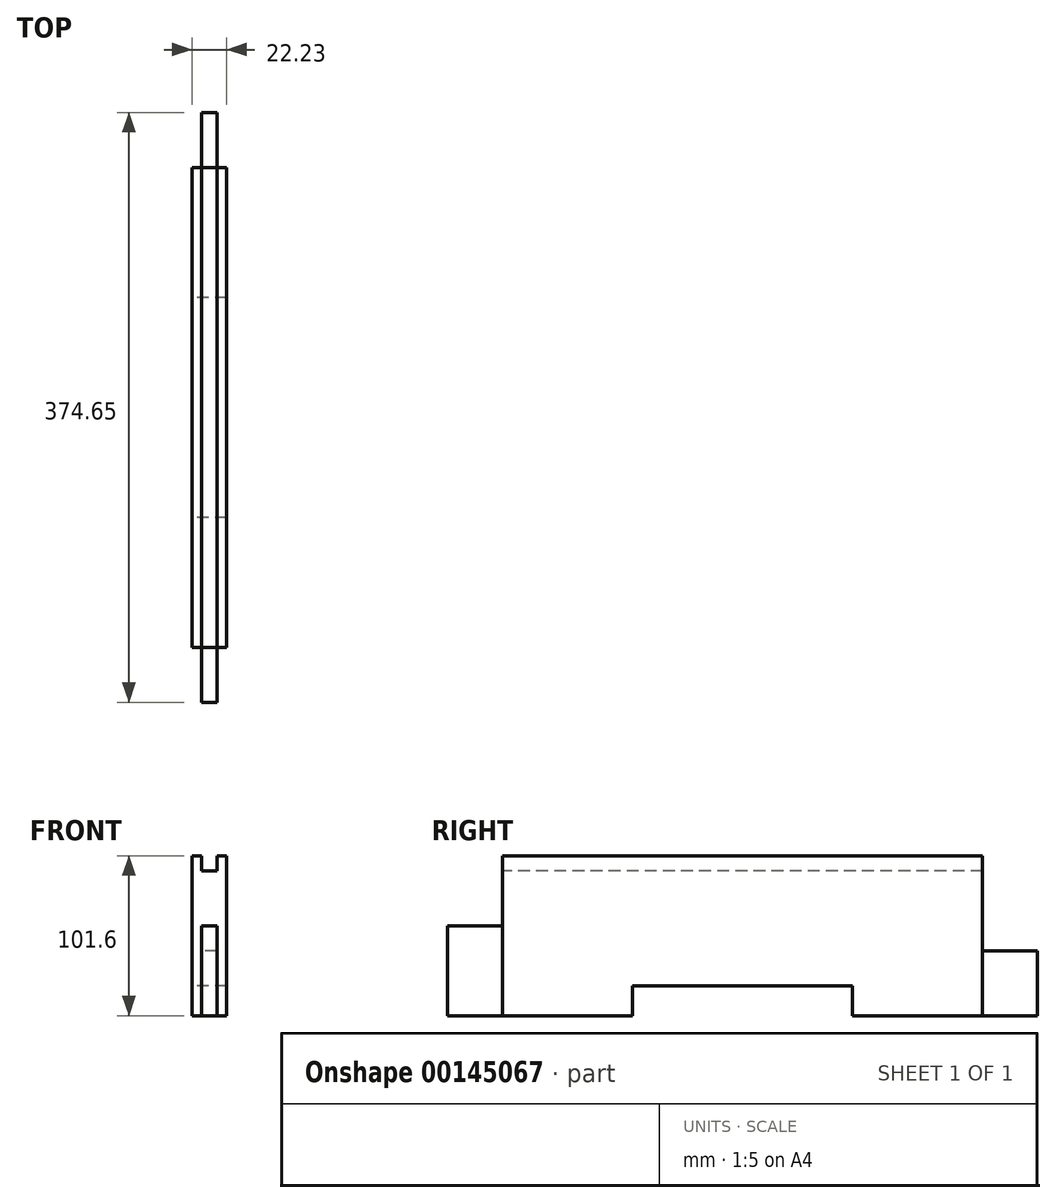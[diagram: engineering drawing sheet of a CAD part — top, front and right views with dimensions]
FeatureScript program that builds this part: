
annotation { "Feature Type Name" : "Feature", "Feature Type Description" : "" }
export const myFeature = defineFeature(function(context is Context, id is Id, definition is map)
    precondition{}
    {
        {
            var Q0;
            Q0=qCreatedBy(makeId("Right.planeOp"),FACE);
            var sketch = newSketch(context, id + "F0", { "sketchPlane" : qUnion([Q0])});
            skLineSegment(sketch, "E0.bottom", {"start": v(0, 0) * mm, "end": v(374.65, 0) * mm});
            skLineSegment(sketch, "E0.top", {"start": v(0, 101.6) * mm, "end": v(374.65, 101.6) * mm});
            skLineSegment(sketch, "E0.left", {"start": v(0, 0) * mm, "end": v(0, 101.6) * mm});
            skLineSegment(sketch, "E0.right", {"start": v(374.65, 0) * mm, "end": v(374.65, 101.6) * mm});
            skSolve(sketch);
        }
        {
            var Q0;
            Q0=makeQuery(id+"F0.imprint","IMPRINT",FACE,{"disambiguationData":[TD([[makeQuery(id+"F0.imprint","IMPRINT",EDGE,{"derivedFrom":sQuery(id+"F0.wireOp",EDGE,"E0.bottom")}),1.0]])]});
            extrude(context, id + "F1", {"entities" : qUnion([Q0]), "depth" : 22.22 * mm, "offsetDistance" : 25.4 * mm});
        }
        {
            var Q0;
            Q0=makeQuery(id+"F1.opExtrude","SWEPT_FACE",FACE,{"disambiguationData":[OSD([sQuery(id+"F0.wireOp",EDGE,"E0.top")])]});
            var sketch = newSketch(context, id + "F2", { "sketchPlane" : qUnion([Q0])});
            skLineSegment(sketch, "E1.bottom", {"start": v(15.87, 374.65) * mm, "end": v(6.35, 374.65) * mm});
            skLineSegment(sketch, "E1.top", {"start": v(15.88, 0) * mm, "end": v(6.35, 0) * mm});
            skLineSegment(sketch, "E1.left", {"start": v(15.87, 374.65) * mm, "end": v(15.88, 0) * mm});
            skLineSegment(sketch, "E1.right", {"start": v(6.35, 374.65) * mm, "end": v(6.35, 0) * mm});
            skLineSegment(sketch, "E2", {"start": v(22.23, 339.73) * mm, "end": v(0, 339.73) * mm});
            skLineSegment(sketch, "E3", {"start": v(22.23, 34.93) * mm, "end": v(0, 34.93) * mm});
            skSolve(sketch);
        }
        {
            var Q0;
            {var subQ0=sQuery(id+"F2.wireOp",EDGE,"E1.bottom");Q0=makeQuery(id+"F2.imprint","IMPRINT",FACE,{"disambiguationData":[TD([[makeQuery(id+"F2.imprint","IMPRINT",EDGE,{"derivedFrom":subQ0}),1.0]])]});}
            var Q1;
            {var subQ0=sQuery(id+"F2.wireOp",EDGE,"E2");var subQ1=sQuery(id+"F2.wireOp",EDGE,"E1.left");var subQ2=makeQuery(id+"F2.imprint","INTERSECT",VERTEX,{"derivedFrom":[subQ1,subQ0]});Q1=makeQuery(id+"F2.imprint","IMPRINT",FACE,{"disambiguationData":[TD([[makeQuery(id+"F2.imprint","IMPRINT",EDGE,{"disambiguationData":[TD([[subQ2,-1.0]])],"derivedFrom":subQ1}),-1.0]])]});}
            var Q2;
            {var subQ0=sQuery(id+"F2.wireOp",EDGE,"E1.top");Q2=makeQuery(id+"F2.imprint","IMPRINT",FACE,{"disambiguationData":[TD([[makeQuery(id+"F2.imprint","IMPRINT",EDGE,{"derivedFrom":subQ0}),-1.0]])]});}
            extrude(context, id + "F3", {"entities" : qUnion([Q0, Q1, Q2]), "operationType" : NewBodyOperationType.REMOVE, "oppositeDirection" : true, "depth" : 9.52 * mm});
        }
        {
            var Q0;
            {var subQ1=sQuery(id+"F0.wireOp",EDGE,"E0.top");var subQ4=sQuery(id+"F2.wireOp",EDGE,"E2");var subQ6=makeQuery(id+"F1.opExtrude","CAP_EDGE",EDGE,{"disambiguationData":[OSD([subQ1])],"isStart":false});var subQ7=makeQuery(id+"F2.imprint","INTERSECT",VERTEX,{"derivedFrom":[subQ6,subQ4]});Q0=makeQuery(id+"F2.imprint","IMPRINT",FACE,{"disambiguationData":[TD([[makeQuery(id+"F2.imprint","IMPRINT",EDGE,{"disambiguationData":[TD([[subQ7,-1.0]])],"derivedFrom":subQ4}),-1.0]])]});}
            var Q1;
            {var subQ1=sQuery(id+"F0.wireOp",EDGE,"E0.top");var subQ4=sQuery(id+"F2.wireOp",EDGE,"E2");var subQ6=makeQuery(id+"F1.opExtrude","CAP_EDGE",EDGE,{"disambiguationData":[OSD([subQ1])],"isStart":true});var subQ7=makeQuery(id+"F2.imprint","INTERSECT",VERTEX,{"derivedFrom":[subQ6,subQ4]});Q1=makeQuery(id+"F2.imprint","IMPRINT",FACE,{"disambiguationData":[TD([[makeQuery(id+"F2.imprint","IMPRINT",EDGE,{"disambiguationData":[TD([[subQ7,1.0]])],"derivedFrom":subQ4}),-1.0]])]});}
            var Q2;
            {var subQ1=sQuery(id+"F0.wireOp",EDGE,"E0.top");var subQ4=sQuery(id+"F2.wireOp",EDGE,"E3");var subQ6=makeQuery(id+"F1.opExtrude","CAP_EDGE",EDGE,{"disambiguationData":[OSD([subQ1])],"isStart":true});var subQ7=makeQuery(id+"F2.imprint","INTERSECT",VERTEX,{"derivedFrom":[subQ6,subQ4]});Q2=makeQuery(id+"F2.imprint","IMPRINT",FACE,{"disambiguationData":[TD([[makeQuery(id+"F2.imprint","IMPRINT",EDGE,{"disambiguationData":[TD([[subQ7,1.0]])],"derivedFrom":subQ4}),1.0]])]});}
            var Q3;
            {var subQ1=sQuery(id+"F0.wireOp",EDGE,"E0.top");var subQ4=sQuery(id+"F2.wireOp",EDGE,"E3");var subQ6=makeQuery(id+"F1.opExtrude","CAP_EDGE",EDGE,{"disambiguationData":[OSD([subQ1])],"isStart":false});var subQ8=makeQuery(id+"F2.imprint","INTERSECT",VERTEX,{"derivedFrom":[subQ6,subQ4]});Q3=makeQuery(id+"F2.imprint","IMPRINT",FACE,{"disambiguationData":[TD([[makeQuery(id+"F2.imprint","IMPRINT",EDGE,{"disambiguationData":[TD([[subQ8,-1.0]])],"derivedFrom":subQ4}),1.0]])]});}
            extrude(context, id + "F4", {"entities" : qUnion([Q0, Q1, Q2, Q3]), "operationType" : NewBodyOperationType.REMOVE, "endBound" : BoundingType.UP_TO_NEXT, "oppositeDirection" : true, "depth" : 25.4 * mm});
        }
        {
            var Q0;
            {var subQ0=sQuery(id+"F2.wireOp",EDGE,"E1.right");Q0=makeQuery(id+"F4.boolean.opBoolean","COPY",FACE,{"derivedFrom":makeQuery(id+"F4.opExtrude","SWEPT_FACE",FACE,{"disambiguationData":[OSD([subQ0]),TDD([makeQuery(id+"F2.imprint","IMPRINT",EDGE,{"disambiguationData":[TD([[makeQuery(id+"F2.imprint","INTERSECT",VERTEX,{"derivedFrom":[subQ0,sQuery(id+"F2.wireOp",EDGE,"E2")]}),1.0]])],"derivedFrom":subQ0})])]})});}
            var sketch = newSketch(context, id + "F5", { "sketchPlane" : qUnion([Q0])});
            skLineSegment(sketch, "E4.bottom", {"start": v(-374.65, 92.08) * mm, "end": v(-339.73, 92.08) * mm});
            skLineSegment(sketch, "E4.top", {"start": v(-374.65, 41.27) * mm, "end": v(-339.73, 41.28) * mm});
            skLineSegment(sketch, "E4.left", {"start": v(-374.65, 92.08) * mm, "end": v(-374.65, 41.28) * mm});
            skLineSegment(sketch, "E4.right", {"start": v(-339.73, 92.07) * mm, "end": v(-339.73, 41.28) * mm});
            skLineSegment(sketch, "E5.bottom", {"start": v(0, 92.08) * mm, "end": v(-34.93, 92.08) * mm});
            skLineSegment(sketch, "E5.top", {"start": v(0, 41.28) * mm, "end": v(-34.92, 41.28) * mm});
            skLineSegment(sketch, "E5.left", {"start": v(0, 92.08) * mm, "end": v(0, 41.28) * mm});
            skLineSegment(sketch, "E5.right", {"start": v(-34.93, 92.08) * mm, "end": v(-34.92, 41.28) * mm});
            skSolve(sketch);
        }
        {
            var Q0;
            Q0=makeQuery(id+"F5.imprint","IMPRINT",FACE,{"disambiguationData":[TD([[makeQuery(id+"F5.imprint","IMPRINT",EDGE,{"derivedFrom":sQuery(id+"F5.wireOp",EDGE,"E4.bottom")}),-1.0]])]});
            var Q1;
            Q1=makeQuery(id+"F5.imprint","IMPRINT",FACE,{"disambiguationData":[TD([[makeQuery(id+"F5.imprint","IMPRINT",EDGE,{"derivedFrom":sQuery(id+"F5.wireOp",EDGE,"E5.bottom")}),1.0]])]});
            extrude(context, id + "F6", {"entities" : qUnion([Q0, Q1]), "operationType" : NewBodyOperationType.REMOVE, "endBound" : BoundingType.UP_TO_NEXT, "oppositeDirection" : true, "depth" : 25.4 * mm});
        }
        {
            var Q0;
            Q0=qCreatedBy(makeId("Right.planeOp"),FACE);
            var sketch = newSketch(context, id + "F7", { "sketchPlane" : qUnion([Q0])});
            skLineSegment(sketch, "E6.bottom", {"start": v(257.18, 19.05) * mm, "end": v(212.73, 19.05) * mm});
            skLineSegment(sketch, "E6.top", {"start": v(257.18, 0) * mm, "end": v(117.48, 0) * mm});
            skLineSegment(sketch, "E6.left", {"start": v(257.18, 19.05) * mm, "end": v(257.18, 0) * mm});
            skLineSegment(sketch, "E6.right", {"start": v(117.48, 19.05) * mm, "end": v(117.48, 0) * mm});
            skLineSegment(sketch, "E7.trimOffspring", {"start": v(161.93, 19.05) * mm, "end": v(117.48, 19.05) * mm});
            skLineSegment(sketch, "E8", {"start": v(161.93, 19.05) * mm, "end": v(212.73, 19.05) * mm});
            skSolve(sketch);
        }
        {
            var Q0;
            Q0=makeQuery(id+"F7.imprint","IMPRINT",FACE,{"disambiguationData":[TD([[makeQuery(id+"F7.imprint","IMPRINT",EDGE,{"derivedFrom":sQuery(id+"F7.wireOp",EDGE,"E6.bottom")}),1.0]])]});
            extrude(context, id + "F8", {"entities" : qUnion([Q0]), "operationType" : NewBodyOperationType.REMOVE, "endBound" : BoundingType.UP_TO_NEXT, "depth" : 25.4 * mm});
        }
        {
            var Q0;
            Q0=makeQuery(id+"F6.boolean.opBoolean","COPY",FACE,{"derivedFrom":makeQuery(id+"F6.opExtrude","SWEPT_FACE",FACE,{"disambiguationData":[OSD([sQuery(id+"F5.wireOp",EDGE,"E5.top")])]})});
            extrude(context, id + "F9", {"entities" : qUnion([Q0]), "operationType" : NewBodyOperationType.ADD, "depth" : 15.88 * mm});
        }
    });
